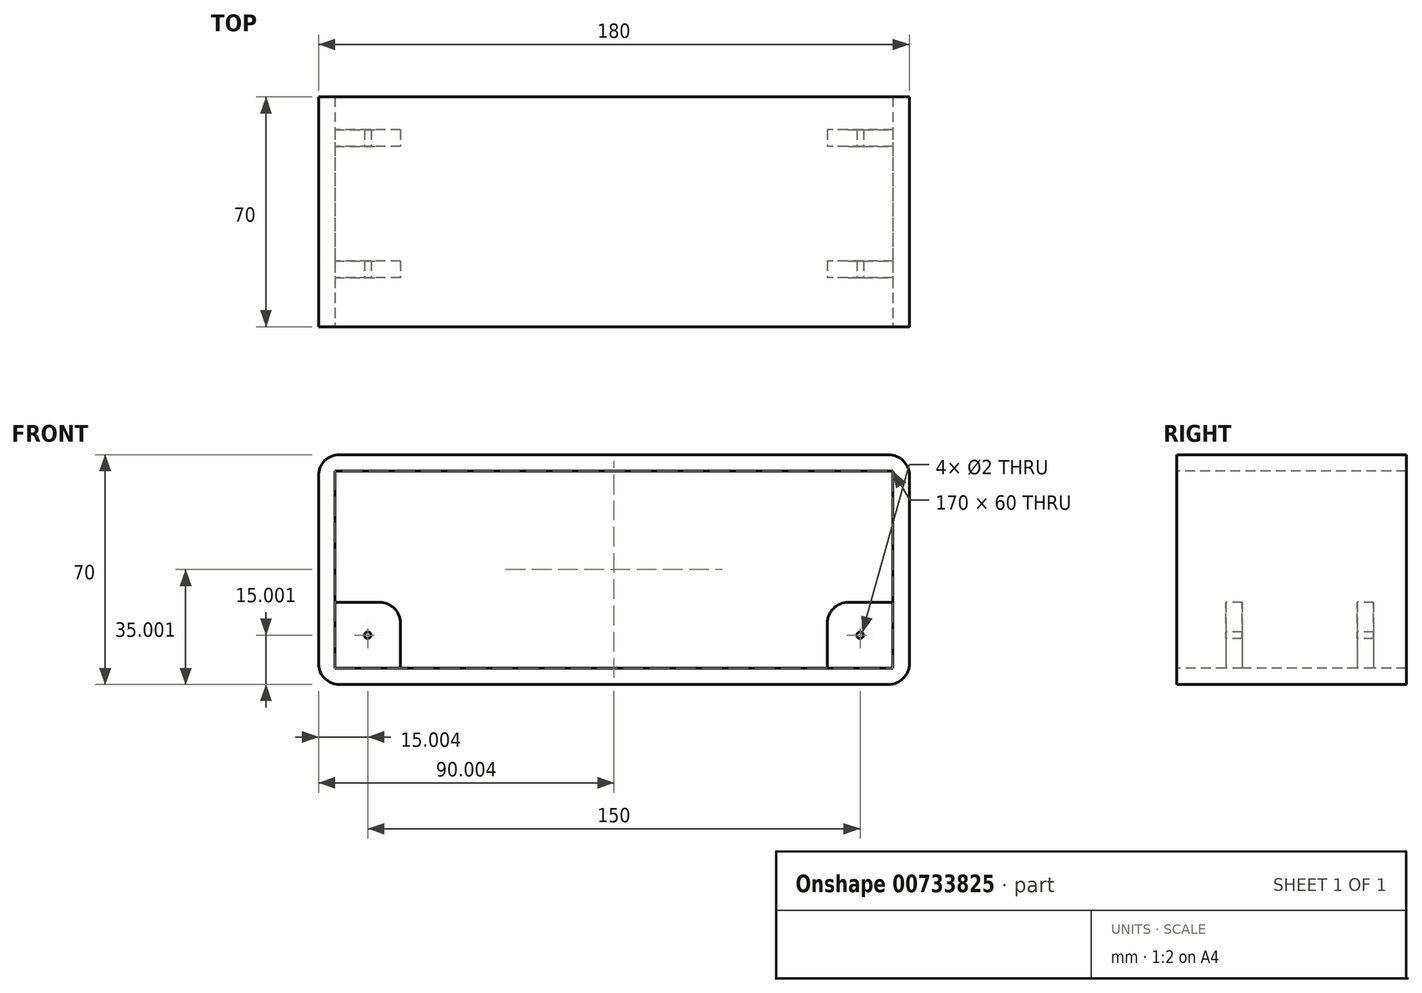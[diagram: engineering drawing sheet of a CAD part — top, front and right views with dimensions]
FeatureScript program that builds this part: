
annotation { "Feature Type Name" : "Feature", "Feature Type Description" : "" }
export const myFeature = defineFeature(function(context is Context, id is Id, definition is map)
    precondition{}
    {
        {
            var Q0;
            Q0=qCreatedBy(makeId("Front.planeOp"),FACE);
            var sketch = newSketch(context, id + "F0", { "sketchPlane" : qUnion([Q0])});
            skLineSegment(sketch, "E0", {"start": v(-86.1, 41.5) * mm, "end": v(81.2, 41.5) * mm});
            skLineSegment(sketch, "E1", {"start": v(87.55, 35.15) * mm, "end": v(87.55, -22.15) * mm});
            skLineSegment(sketch, "E2", {"start": v(81.2, -28.5) * mm, "end": v(-86.1, -28.5) * mm});
            skLineSegment(sketch, "E3", {"start": v(-92.45, -22.15) * mm, "end": v(-92.45, 35.15) * mm});
            skArc(sketch, "E4.filletArc", {"start": v(-86.1, 41.5) * mm, "mid": v(-90.59, 39.64) * mm, "end": v(-92.45, 35.15) * mm});
            skPoint(sketch, "E5.visualSharp", {"position": v(-92.45, -28.5) * mm});
            skArc(sketch, "E5.filletArc", {"start": v(-92.45, -22.15) * mm, "mid": v(-90.59, -26.64) * mm, "end": v(-86.1, -28.5) * mm});
            skPoint(sketch, "E6.visualSharp", {"position": v(87.55, -28.5) * mm});
            skArc(sketch, "E6.filletArc", {"start": v(81.2, -28.5) * mm, "mid": v(85.7, -26.64) * mm, "end": v(87.55, -22.15) * mm});
            skPoint(sketch, "E7.visualSharp", {"position": v(87.55, 41.5) * mm});
            skArc(sketch, "E7.filletArc", {"start": v(87.55, 35.15) * mm, "mid": v(85.7, 39.64) * mm, "end": v(81.2, 41.5) * mm});
            skPoint(sketch, "E8.visualSharp", {"position": v(82.55, 36.5) * mm});
            skPoint(sketch, "E9.visualSharp", {"position": v(-67.45, -23.5) * mm});
            skPoint(sketch, "E10.visualSharp", {"position": v(-87.45, 36.5) * mm});
            skLineSegment(sketch, "E11.0", {"start": v(-87.45, 36.5) * mm, "end": v(82.55, 36.5) * mm});
            skLineSegment(sketch, "E11.1", {"start": v(-87.45, -23.5) * mm, "end": v(-87.45, 36.5) * mm});
            skLineSegment(sketch, "E11.2", {"start": v(82.55, -23.5) * mm, "end": v(-87.45, -23.5) * mm});
            skLineSegment(sketch, "E11.3", {"start": v(82.55, 36.5) * mm, "end": v(82.55, -23.5) * mm});
            skLineSegment(sketch, "E12.bottom", {"start": v(-87.45, -3.5) * mm, "end": v(-73.8, -3.5) * mm});
            skLineSegment(sketch, "E12.top", {"start": v(-87.45, -23.5) * mm, "end": v(-67.45, -23.5) * mm});
            skLineSegment(sketch, "E12.left", {"start": v(-67.45, -9.85) * mm, "end": v(-67.45, -23.5) * mm});
            skLineSegment(sketch, "E12.right", {"start": v(-87.45, -3.5) * mm, "end": v(-87.45, -23.5) * mm});
            skCircle(sketch, "E13", {"center": v(-77.45, -13.5) * mm, "radius": 1 * mm});
            skPoint(sketch, "E14", {"position": v(-77.45, -3.5) * mm});
            skPoint(sketch, "E15", {"position": v(-67.45, -13.5) * mm});
            skLineSegment(sketch, "E16.bottom", {"start": v(-87.45, 36.5) * mm, "end": v(-67.45, 36.5) * mm});
            skLineSegment(sketch, "E16.top", {"start": v(-87.45, 16.5) * mm, "end": v(-73.8, 16.5) * mm});
            skLineSegment(sketch, "E16.left", {"start": v(-67.45, 36.5) * mm, "end": v(-67.45, 22.85) * mm});
            skLineSegment(sketch, "E16.right", {"start": v(-87.45, 36.5) * mm, "end": v(-87.45, 16.5) * mm});
            skCircle(sketch, "E17", {"center": v(-77.45, 26.5) * mm, "radius": 1 * mm});
            skPoint(sketch, "E18", {"position": v(-77.45, 36.5) * mm});
            skPoint(sketch, "E19", {"position": v(-67.45, 26.5) * mm});
            skLineSegment(sketch, "E20.bottom", {"start": v(68.9, -3.5) * mm, "end": v(82.55, -3.5) * mm});
            skLineSegment(sketch, "E20.top", {"start": v(62.55, -23.5) * mm, "end": v(82.55, -23.5) * mm});
            skLineSegment(sketch, "E20.left", {"start": v(62.55, -9.85) * mm, "end": v(62.55, -23.5) * mm});
            skLineSegment(sketch, "E20.right", {"start": v(82.55, -3.5) * mm, "end": v(82.55, -23.5) * mm});
            skCircle(sketch, "E21", {"center": v(72.55, -13.5) * mm, "radius": 1 * mm});
            skPoint(sketch, "E22", {"position": v(72.55, -3.5) * mm});
            skPoint(sketch, "E23", {"position": v(62.55, -13.5) * mm});
            skLineSegment(sketch, "E24.bottom", {"start": v(62.55, 36.5) * mm, "end": v(82.55, 36.5) * mm});
            skLineSegment(sketch, "E24.top", {"start": v(68.9, 16.5) * mm, "end": v(82.55, 16.5) * mm});
            skLineSegment(sketch, "E24.left", {"start": v(62.55, 36.5) * mm, "end": v(62.55, 22.85) * mm});
            skLineSegment(sketch, "E24.right", {"start": v(82.55, 36.5) * mm, "end": v(82.55, 16.5) * mm});
            skCircle(sketch, "E25", {"center": v(72.55, 26.5) * mm, "radius": 1 * mm});
            skPoint(sketch, "E26", {"position": v(72.55, 36.5) * mm});
            skPoint(sketch, "E27", {"position": v(62.55, 26.5) * mm});
            skPoint(sketch, "E28.visualSharp", {"position": v(-67.45, 16.5) * mm});
            skArc(sketch, "E28.filletArc", {"start": v(-73.8, 16.5) * mm, "mid": v(-69.3, 18.36) * mm, "end": v(-67.45, 22.85) * mm});
            skPoint(sketch, "E29.visualSharp", {"position": v(-67.45, -3.5) * mm});
            skArc(sketch, "E29.filletArc", {"start": v(-67.45, -9.85) * mm, "mid": v(-69.3, -5.36) * mm, "end": v(-73.8, -3.5) * mm});
            skPoint(sketch, "E30.visualSharp", {"position": v(62.55, -3.5) * mm});
            skArc(sketch, "E30.filletArc", {"start": v(68.9, -3.5) * mm, "mid": v(64.41, -5.36) * mm, "end": v(62.55, -9.85) * mm});
            skPoint(sketch, "E31.visualSharp", {"position": v(62.55, 16.5) * mm});
            skArc(sketch, "E31.filletArc", {"start": v(62.55, 22.85) * mm, "mid": v(64.41, 18.36) * mm, "end": v(68.9, 16.5) * mm});
            skLineSegment(sketch, "E32.bottom", {"start": v(-11.58, -51.78) * mm, "end": v(48.42, -51.78) * mm});
            skLineSegment(sketch, "E32.top", {"start": v(-11.58, -111.78) * mm, "end": v(48.42, -111.78) * mm});
            skLineSegment(sketch, "E32.left", {"start": v(-11.58, -51.78) * mm, "end": v(-11.58, -111.78) * mm});
            skLineSegment(sketch, "E32.right", {"start": v(48.42, -51.78) * mm, "end": v(48.42, -111.78) * mm});
            skCircle(sketch, "E33", {"center": v(18.42, -81.78) * mm, "radius": 25 * mm});
            skPoint(sketch, "E34", {"position": v(-11.58, -81.78) * mm});
            skPoint(sketch, "E35", {"position": v(18.42, -51.78) * mm});
            skCircle(sketch, "E36", {"center": v(-101.38, -76.06) * mm, "radius": 2.5 * mm});
            skCircle(sketch, "E37", {"center": v(-151.38, -76.06) * mm, "radius": 2.5 * mm});
            skCircle(sketch, "E38", {"center": v(-151.38, -26.06) * mm, "radius": 2.5 * mm});
            skCircle(sketch, "E39", {"center": v(-101.38, -26.06) * mm, "radius": 2.5 * mm});
            skLineSegment(sketch, "E40.bottom", {"start": v(-67.45, 36.5) * mm, "end": v(-7.45, 36.5) * mm});
            skLineSegment(sketch, "E40.top", {"start": v(-67.45, -23.5) * mm, "end": v(-7.45, -23.5) * mm});
            skLineSegment(sketch, "E40.left", {"start": v(-67.45, 36.5) * mm, "end": v(-67.45, -23.5) * mm});
            skLineSegment(sketch, "E40.right", {"start": v(-7.45, 36.5) * mm, "end": v(-7.45, -23.5) * mm});
            skCircle(sketch, "E41", {"center": v(-37.45, 6.5) * mm, "radius": 25 * mm});
            skPoint(sketch, "E42", {"position": v(-67.45, 6.5) * mm});
            skPoint(sketch, "E43", {"position": v(-37.45, 36.5) * mm});
            skCircle(sketch, "E44", {"center": v(-12.78, 31.5) * mm, "radius": 1 * mm});
            skCircle(sketch, "E45", {"center": v(-62.45, 31.5) * mm, "radius": 1 * mm});
            skCircle(sketch, "E46", {"center": v(-12.45, -18.5) * mm, "radius": 1 * mm});
            skCircle(sketch, "E47", {"center": v(-62.45, -18.5) * mm, "radius": 1 * mm});
            skLineSegment(sketch, "E48", {"start": v(-7.45, -23.5) * mm, "end": v(-12.45, -23.5) * mm});
            skLineSegment(sketch, "E49", {"start": v(-67.45, -23.5) * mm, "end": v(-62.45, -23.5) * mm});
            skLineSegment(sketch, "E50", {"start": v(-67.45, -18.5) * mm, "end": v(-67.45, -23.5) * mm});
            skLineSegment(sketch, "E51", {"start": v(-7.45, 31.5) * mm, "end": v(-7.45, 36.5) * mm});
            skLineSegment(sketch, "E52", {"start": v(-67.45, 36.5) * mm, "end": v(-62.45, 36.5) * mm});
            skSolve(sketch);
        }
        {
            var Q0;
            Q0=makeQuery(id+"F0.imprint","IMPRINT",FACE,{"disambiguationData":[TD([[makeQuery(id+"F0.imprint","IMPRINT",EDGE,{"derivedFrom":sQuery(id+"F0.wireOp",EDGE,"E0")}),-1.0]])]});
            extrude(context, id + "F1", {"entities" : qUnion([Q0]), "oppositeDirection" : true, "depth" : 70 * mm, "offsetDistance" : 25.4 * mm});
        }
        {
            var Q0;
            Q0=makeQuery(id+"F0.imprint","IMPRINT",FACE,{"disambiguationData":[TD([[makeQuery(id+"F0.imprint","IMPRINT",EDGE,{"derivedFrom":sQuery(id+"F0.wireOp",EDGE,"E12.bottom")}),-1.0]])]});
            var Q1;
            Q1=makeQuery(id+"F0.imprint","IMPRINT",FACE,{"disambiguationData":[TD([[makeQuery(id+"F0.imprint","IMPRINT",EDGE,{"derivedFrom":sQuery(id+"F0.wireOp",EDGE,"E20.bottom")}),-1.0]])]});
            var Q2;
            Q2=makeQuery(id+"F0.imprint","IMPRINT",FACE,{"disambiguationData":[TD([[makeQuery(id+"F0.imprint","IMPRINT",EDGE,{"derivedFrom":sQuery(id+"F0.wireOp",EDGE,"E24.bottom")}),-1.0]])]});
            var Q3;
            Q3=makeQuery(id+"F0.imprint","IMPRINT",FACE,{"disambiguationData":[TD([[makeQuery(id+"F0.imprint","IMPRINT",EDGE,{"derivedFrom":sQuery(id+"F0.wireOp",EDGE,"E16.bottom")}),-1.0]])]});
            extrude(context, id + "F2", {"entities" : qUnion([Q0, Q1, Q2, Q3]), "operationType" : NewBodyOperationType.ADD, "oppositeDirection" : true, "depth" : 20 * mm, "offsetDistance" : 25.4 * mm, "hasSecondDirection" : true, "secondDirectionOppositeDirection" : false, "secondDirectionDepth" : -15 * mm});
        }
        {
            var Q0;
            Q0=makeQuery(id+"F0.imprint","IMPRINT",FACE,{"disambiguationData":[TD([[makeQuery(id+"F0.imprint","IMPRINT",EDGE,{"derivedFrom":sQuery(id+"F0.wireOp",EDGE,"E24.bottom")}),-1.0]])]});
            var Q1;
            Q1=makeQuery(id+"F0.imprint","IMPRINT",FACE,{"disambiguationData":[TD([[makeQuery(id+"F0.imprint","IMPRINT",EDGE,{"derivedFrom":sQuery(id+"F0.wireOp",EDGE,"E20.bottom")}),-1.0]])]});
            var Q2;
            Q2=makeQuery(id+"F0.imprint","IMPRINT",FACE,{"disambiguationData":[TD([[makeQuery(id+"F0.imprint","IMPRINT",EDGE,{"derivedFrom":sQuery(id+"F0.wireOp",EDGE,"E12.bottom")}),-1.0]])]});
            var Q3;
            Q3=makeQuery(id+"F0.imprint","IMPRINT",FACE,{"disambiguationData":[TD([[makeQuery(id+"F0.imprint","IMPRINT",EDGE,{"derivedFrom":sQuery(id+"F0.wireOp",EDGE,"E16.bottom")}),-1.0]])]});
            extrude(context, id + "F3", {"entities" : qUnion([Q0, Q1, Q2, Q3]), "operationType" : NewBodyOperationType.ADD, "oppositeDirection" : true, "depth" : 60 * mm, "offsetDistance" : 25.4 * mm, "hasSecondDirection" : true, "secondDirectionOppositeDirection" : true, "secondDirectionDepth" : 55 * mm});
        }
    });
